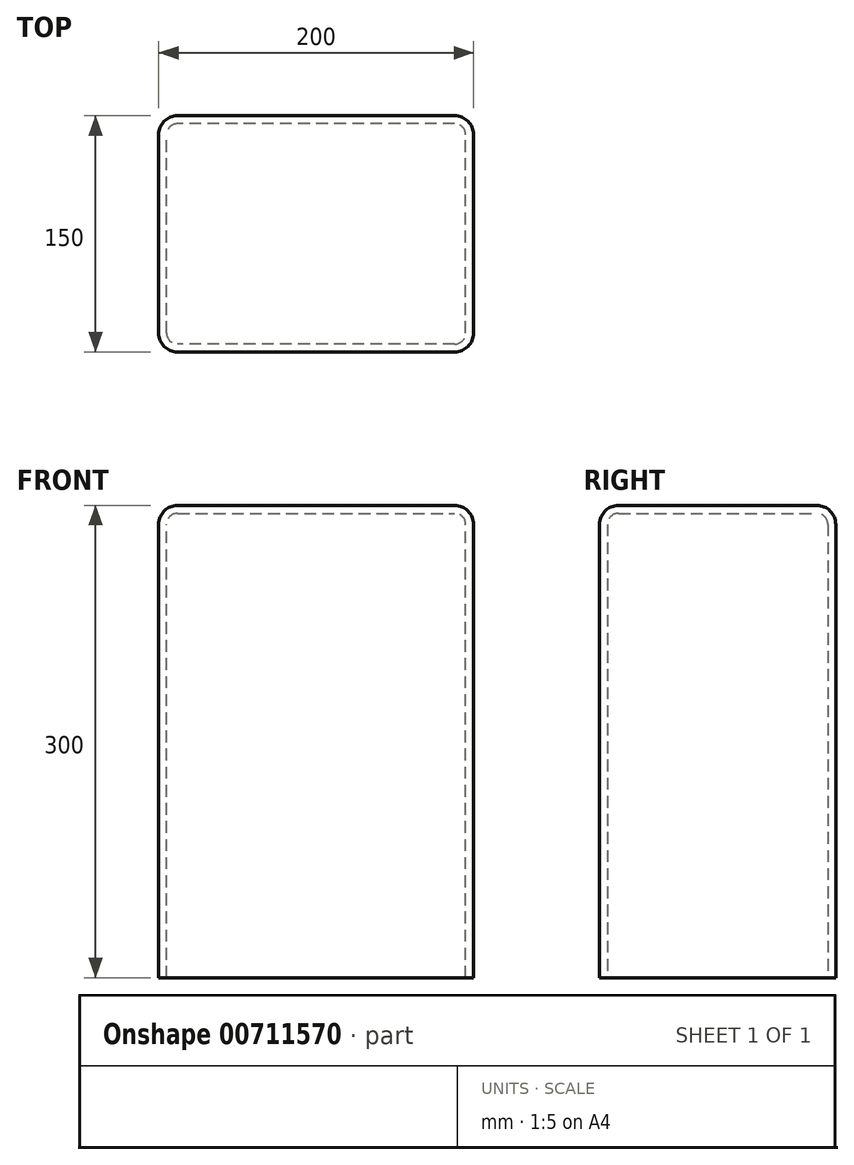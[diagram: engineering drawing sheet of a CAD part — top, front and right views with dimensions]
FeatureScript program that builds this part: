
annotation { "Feature Type Name" : "Feature", "Feature Type Description" : "" }
export const myFeature = defineFeature(function(context is Context, id is Id, definition is map)
    precondition{}
    {
        {
            var Q0;
            Q0=qCreatedBy(makeId("Top.planeOp"),FACE);
            var sketch = newSketch(context, id + "F0", { "sketchPlane" : qUnion([Q0])});
            skLineSegment(sketch, "E0.bottom", {"start": v(100, -75) * mm, "end": v(-100, -75) * mm});
            skLineSegment(sketch, "E0.top", {"start": v(100, 75) * mm, "end": v(-100, 75) * mm});
            skLineSegment(sketch, "E0.left", {"start": v(100, -75) * mm, "end": v(100, 75) * mm});
            skLineSegment(sketch, "E0.right", {"start": v(-100, -75) * mm, "end": v(-100, 75) * mm});
            skPoint(sketch, "E0.middle", {"position": v(0, 0) * mm});
            skSolve(sketch);
        }
        {
            var Q0;
            Q0=makeQuery(id+"F0.imprint","IMPRINT",FACE,{"disambiguationData":[TD([[makeQuery(id+"F0.imprint","IMPRINT",EDGE,{"derivedFrom":sQuery(id+"F0.wireOp",EDGE,"E0.bottom")}),-1.0]])]});
            extrude(context, id + "F1", {"entities" : qUnion([Q0]), "depth" : 300 * mm, "offsetDistance" : 25.4 * mm});
        }
        {
            var Q0;
            Q0=makeQuery(id+"F1.opExtrude","SWEPT_EDGE",EDGE,{"disambiguationData":[OSD([sQuery(id+"F0.wireOp",EDGE,"E0.top"),sQuery(id+"F0.wireOp",EDGE,"E0.right")])]});
            var Q1;
            Q1=makeQuery(id+"F1.opExtrude","CAP_EDGE",EDGE,{"disambiguationData":[OSD([sQuery(id+"F0.wireOp",EDGE,"E0.right")])],"isStart":false});
            var Q2;
            Q2=makeQuery(id+"F1.opExtrude","SWEPT_EDGE",EDGE,{"disambiguationData":[OSD([sQuery(id+"F0.wireOp",EDGE,"E0.bottom"),sQuery(id+"F0.wireOp",EDGE,"E0.right")])]});
            var Q3;
            Q3=makeQuery(id+"F1.opExtrude","CAP_EDGE",EDGE,{"disambiguationData":[OSD([sQuery(id+"F0.wireOp",EDGE,"E0.bottom")])],"isStart":false});
            var Q4;
            Q4=makeQuery(id+"F1.opExtrude","CAP_EDGE",EDGE,{"disambiguationData":[OSD([sQuery(id+"F0.wireOp",EDGE,"E0.left")])],"isStart":false});
            var Q5;
            Q5=makeQuery(id+"F1.opExtrude","SWEPT_EDGE",EDGE,{"disambiguationData":[OSD([sQuery(id+"F0.wireOp",EDGE,"E0.bottom"),sQuery(id+"F0.wireOp",EDGE,"E0.left")])]});
            var Q6;
            Q6=makeQuery(id+"F1.opExtrude","SWEPT_EDGE",EDGE,{"disambiguationData":[OSD([sQuery(id+"F0.wireOp",EDGE,"E0.top"),sQuery(id+"F0.wireOp",EDGE,"E0.left")])]});
            var Q7;
            Q7=makeQuery(id+"F1.opExtrude","CAP_EDGE",EDGE,{"disambiguationData":[OSD([sQuery(id+"F0.wireOp",EDGE,"E0.top")])],"isStart":false});
            fillet(context, id + "F2", {"entities" : qUnion([Q0, Q1, Q2, Q3, Q4, Q5, Q6, Q7]), "radius" : 12 * mm, "tangentPropagation" : true, "allowEdgeOverflow" : false});
        }
        {
            var Q0;
            Q0=makeQuery(id+"F1.opExtrude","CAP_FACE",FACE,{"disambiguationData":[OSD([sQuery(id+"F0.wireOp",EDGE,"E0.bottom"),sQuery(id+"F0.wireOp",EDGE,"E0.top"),sQuery(id+"F0.wireOp",EDGE,"E0.left"),sQuery(id+"F0.wireOp",EDGE,"E0.right")])],"isStart":true});
            shell(context, id + "F3", {"entities" : qUnion([Q0]), "thickness" : 5 * mm});
        }
    });
